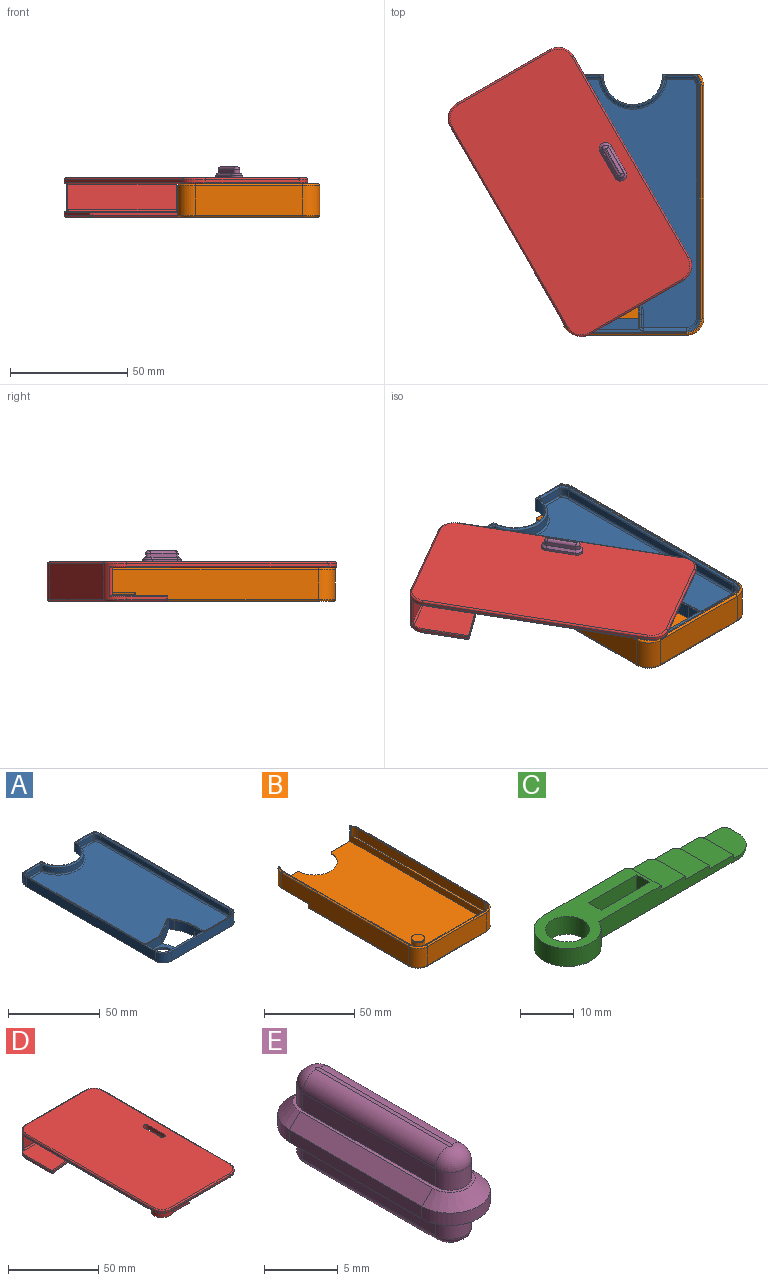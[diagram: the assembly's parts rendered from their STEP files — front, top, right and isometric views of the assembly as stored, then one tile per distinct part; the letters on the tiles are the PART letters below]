
ASSEMBLY  parts=5 mates=4
PART A: 95 faces, bbox 59.1x110.7x6.4 mm
  f0: plane 11.32x3.56mm, normal (0,-1,0), area 40.3mm2, adj f78,f79,f87,f88
  f1: plane 99.19x6.35mm, normal (1,0,0), area 629.8mm2, adj f4,f6,f36,f40
  f2: plane 15.05x6.35mm, normal (0,1,0), area 95.6mm2, adj f4,f6,f31,f37
  f3: plane 99.19x6.35mm, normal (-1,0,0), area 629.8mm2, adj f4,f6,f35,f38
  f4: plane 109.98x58.04mm, normal (0,0,-1), area 5827mm2, adj f1,f2,f3,f5,f14,f16,f17,f18
  f5: plane 15.05x6.35mm, normal (0,1,0), area 95.6mm2, adj f4,f6,f31,f41
  f6: plane 109.98x58.04mm, normal (0,0,1), area 233.7mm2, adj f1,f2,f3,f5,f11,f13,f14,f19
  f7: plane 11.32x3.56mm, normal (0,-1,0), area 40.3mm2, adj f55,f56,f66,f67
  f8: plane 105.92x53.98mm, normal (0,0,1), area 4899.9mm2, adj f44,f46,f47,f54,f55,f59,f64,f65
  f9: plane 30.16x12.91mm, normal (0,0,1), area 175.1mm2, adj f11,f13,f16,f17,f18,f19,f23,f29
  f10: plane 89.01x3.56mm, normal (1,0,0), area 316.5mm2, adj f39,f44,f45,f51
  f11: plane 25.4x5.08mm, normal (0,1,0), area 129mm2, adj f6,f9,f19,f33
  f12: plane 99.19x3.56mm, normal (-1,0,0), area 352.7mm2, adj f34,f42,f71,f94
  f13: plane 8.15x5.08mm, normal (1,0,0), area 41.4mm2, adj f6,f9,f29,f33
  f14: plane 45.97x6.35mm, normal (0,-1,0), area 291.9mm2, adj f4,f6,f35,f36
  f15: plane 18.54x3.56mm, normal (0,1,0), area 65.9mm2, adj f34,f76,f86,f91
  f16: cylinder r=7.62mm len=3.81mm, axis (0,0,1), area 5.1mm2, adj f4,f9,f17,f23
  f17: plane 1.59x1.27mm, normal (1,0,0), area 2mm2, adj f4,f9,f16,f18
  f18: plane 16.19x1.27mm, normal (0,1,0), area 20.6mm2, adj f4,f9,f17,f19
  f19: plane 6.35x6.35mm, normal (-1,0,0), area 34.3mm2, adj f4,f6,f9,f11,f18,f20
  f20: cylinder r=23.81mm len=11.91mm, axis (0,0,1), area 79.2mm2, adj f4,f6,f19,f21
  f21: plane 6.35x2.75mm, normal (-0.87,-0.5,0), area 20.2mm2, adj f4,f6,f20,f22
  f22: plane 14.02x8.1mm, normal (0.5,-0.87,0), area 102.8mm2, adj f4,f6,f21,f23,f29
  f23: plane 2.75x1.59mm, normal (0.87,0.5,0), area 4mm2, adj f4,f9,f16,f22
  f24: plane 5.59x3.56mm, normal (1,0,0), area 19.9mm2, adj f25,f75,f85,f86
  f25: cylinder r=25.08mm len=12.54mm, axis (0,0,-1), area 46.7mm2, adj f24,f26,f69,f81
  f26: plane 3.56x3.19mm, normal (0.87,0.5,0), area 13.1mm2, adj f25,f63,f64,f74
  f27: plane 13.99x8.08mm, normal (-0.5,0.87,0), area 57.5mm2, adj f53,f54,f62,f63
  f28: plane 10.06x3.56mm, normal (0,1,0), area 35.8mm2, adj f45,f46,f52,f53
  f29: plane 11.36x5.08mm, normal (0,-1,0), area 57.7mm2, adj f6,f9,f13,f22
  f30: cylinder r=4.76mm len=9.53mm, axis (0,0,1), area 38mm2, adj f4,f9
  f31: cylinder r=12.7mm len=25.4mm, axis (0,0,1), area 253.4mm2, adj f2,f4,f5,f6
  f32: cylinder r=13.97mm len=27.67mm, axis (0,0,-1), area 142.3mm2, adj f65,f66,f79,f80
  f33: cylinder r=4.76mm len=5.08mm, axis (0,0,1), area 38mm2, adj f6,f9,f11,f13
  f34: cylinder r=4.76mm len=4.76mm, axis (0,0,-1), area 26.6mm2, adj f12,f15,f70,f93
  f35: cylinder r=6.03mm len=6.35mm, axis (0,0,-1), area 60.2mm2, adj f3,f4,f6,f14
  f36: cylinder r=6.03mm len=6.35mm, axis (0,0,1), area 60.2mm2, adj f1,f4,f6,f14
  f37: plane 6.35x1.06mm, normal (-1,0,0), area 6.7mm2, adj f2,f4,f6,f38
  f38: cylinder r=6.03mm len=6.35mm, axis (0,0,-1), area 25.3mm2, adj f3,f4,f6,f37
  f39: cylinder r=4.76mm len=3.56mm, axis (0,0,-1), area 12.7mm2, adj f10,f47,f56,f57
  f40: cylinder r=6.03mm len=6.35mm, axis (0,0,-1), area 25.3mm2, adj f1,f4,f6,f41
  f41: plane 6.35x1.06mm, normal (1,0,0), area 6.7mm2, adj f4,f5,f6,f40
  f42: cylinder r=4.76mm len=3.56mm, axis (0,0,-1), area 12.7mm2, adj f12,f77,f87,f92
  f43: sphere r=0.76mm, area 0.9mm2, adj f44,f45,f46
  f44: cylinder r=0.76mm len=89.01mm, axis (0,1,0), area 106.5mm2, adj f8,f10,f43,f47
  f45: cylinder r=0.76mm len=3.56mm, axis (0,0,-1), area 4.3mm2, adj f10,f28,f43,f48
  f46: cylinder r=0.76mm len=10.06mm, axis (-1,0,0), area 12mm2, adj f8,f28,f43,f49
  f47: torus R=4mm, axis (0,0,1), area 4mm2, adj f8,f39,f44,f50
  f48: torus R=1.52mm, axis (0,0,1), area 2mm2, adj f6,f45,f51,f52
  f49: sphere r=0.76mm, area 0.3mm2, adj f46,f53,f54
  f50: sphere r=0.76mm, area 0.5mm2, adj f47,f55,f56
  f51: cylinder r=0.76mm len=89.01mm, axis (0,-1,0), area 106.5mm2, adj f6,f10,f48,f57
  f52: cylinder r=0.76mm len=10.06mm, axis (1,0,0), area 12mm2, adj f6,f28,f48,f58
  f53: cylinder r=0.76mm len=3.56mm, axis (0,0,1), area 1.4mm2, adj f27,f28,f49,f58
  f54: cylinder r=0.76mm len=14.37mm, axis (-0.87,-0.5,0), area 19.3mm2, adj f8,f27,f49,f59
  f55: cylinder r=0.76mm len=11.32mm, axis (1,0,0), area 13.5mm2, adj f7,f8,f50,f60
  f56: cylinder r=0.76mm len=3.56mm, axis (0,0,-1), area 2.2mm2, adj f7,f39,f50,f61
  f57: torus R=5.52mm, axis (0,0,1), area 4.5mm2, adj f6,f39,f51,f61
  f58: torus R=1.52mm, axis (0,0,1), area 0.7mm2, adj f6,f52,f53,f62
  f59: torus R=1.52mm, axis (0,0,1), area 2mm2, adj f8,f54,f63,f64
  f60: sphere r=0.76mm, area 0.8mm2, adj f55,f65,f66
  f61: torus R=1.52mm, axis (0,0,1), area 1mm2, adj f6,f56,f57,f67
  f62: cylinder r=0.76mm len=14.37mm, axis (0.87,0.5,0), area 19.3mm2, adj f6,f27,f58,f68
  f63: cylinder r=0.76mm len=3.56mm, axis (0,0,-1), area 4.3mm2, adj f26,f27,f59,f68
  f64: cylinder r=0.76mm len=3.57mm, axis (-0.5,0.87,0), area 4.4mm2, adj f8,f26,f59,f69
  f65: torus R=14.73mm, axis (0,0,1), area 48.9mm2, adj f8,f32,f60,f72
  f66: cylinder r=0.76mm len=3.56mm, axis (0,0,-1), area 3.9mm2, adj f7,f32,f60,f73
  f67: cylinder r=0.76mm len=11.32mm, axis (-1,0,0), area 13.5mm2, adj f6,f7,f61,f73
  f68: sphere r=0.76mm, area 0.9mm2, adj f62,f63,f74
  f69: torus R=25.84mm, axis (0,0,1), area 15.9mm2, adj f8,f25,f64,f75
  f70: torus R=4mm, axis (0,0,1), area 8.4mm2, adj f8,f34,f71,f76
  f71: cylinder r=0.76mm len=99.19mm, axis (0,-1,0), area 118.7mm2, adj f8,f12,f70,f77
  f72: sphere r=0.76mm, area 0.8mm2, adj f65,f78,f79
  f73: torus R=1.52mm, axis (0,0,1), area 1.8mm2, adj f6,f66,f67,f80
  f74: cylinder r=0.76mm len=3.57mm, axis (0.5,-0.87,0), area 4.4mm2, adj f6,f26,f68,f81
  f75: cylinder r=0.76mm len=5.59mm, axis (0,1,0), area 6.7mm2, adj f8,f24,f69,f82
  f76: cylinder r=0.76mm len=18.54mm, axis (-1,0,0), area 22.2mm2, adj f8,f15,f70,f82
  f77: torus R=4mm, axis (0,0,1), area 4mm2, adj f8,f42,f71,f83
  f78: cylinder r=0.76mm len=11.32mm, axis (1,0,0), area 13.5mm2, adj f0,f8,f72,f83
  f79: cylinder r=0.76mm len=3.56mm, axis (0,0,-1), area 3.9mm2, adj f0,f32,f72,f84
  f80: torus R=13.21mm, axis (0,0,1), area 47mm2, adj f6,f32,f73,f84
  f81: torus R=24.32mm, axis (0,0,1), area 15.5mm2, adj f6,f25,f74,f85
  f82: sphere r=0.76mm, area 0.9mm2, adj f75,f76,f86
  f83: sphere r=0.76mm, area 0.5mm2, adj f77,f78,f87
  f84: torus R=1.52mm, axis (0,0,1), area 1.8mm2, adj f6,f79,f80,f88
  f85: cylinder r=0.76mm len=5.59mm, axis (0,-1,0), area 6.7mm2, adj f6,f24,f81,f89
  f86: cylinder r=0.76mm len=3.56mm, axis (0,0,1), area 4.3mm2, adj f15,f24,f82,f89
  f87: cylinder r=0.76mm len=3.56mm, axis (0,0,-1), area 2.2mm2, adj f0,f42,f83,f90
  f88: cylinder r=0.76mm len=11.32mm, axis (-1,0,0), area 13.5mm2, adj f0,f6,f84,f90
  f89: torus R=1.52mm, axis (0,0,1), area 2mm2, adj f6,f85,f86,f91
  f90: torus R=1.52mm, axis (0,0,1), area 1mm2, adj f6,f87,f88,f92
  f91: cylinder r=0.76mm len=18.54mm, axis (1,0,0), area 22.2mm2, adj f6,f15,f89,f93
  f92: torus R=5.52mm, axis (0,0,1), area 4.5mm2, adj f6,f42,f90,f94
  f93: torus R=5.52mm, axis (0,0,1), area 9.5mm2, adj f6,f34,f91,f94
  f94: cylinder r=0.76mm len=99.19mm, axis (0,1,0), area 118.7mm2, adj f6,f12,f92,f93
PART B: 65 faces, bbox 61.8x112.7x14.2 mm
  f0: torus R=3.08mm, axis (0,0,1), area 13.2mm2, adj f28,f64
  f1: plane 14.74x10.71mm, normal (0,1,0), area 8.7mm2, adj f9,f12,f48,f55,f60,f61
  f2: plane 14.74x10.71mm, normal (0,1,0), area 8.7mm2, adj f9,f11,f39,f40,f41,f44
  f3: plane 99.19x6.35mm, normal (1,0,0), area 629.8mm2, adj f5,f6,f19,f26
  f4: plane 99.19x6.35mm, normal (-1,0,0), area 629.8mm2, adj f5,f6,f20,f25
  f5: plane 109.18x58.04mm, normal (0,0,1), area 338.3mm2, adj f3,f4,f10,f11,f12,f15,f17,f18
  f6: plane 110.21x59.06mm, normal (0,0,1), area 138.7mm2, adj f3,f4,f11,f12,f15,f19,f20,f25
  f7: plane 59.06x24.56mm, normal (0,0,-1), area 999.9mm2, adj f16,f30,f32,f41,f49,f50,f53,f55
  f8: plane 99.19x12.7mm, normal (-1,0,0), area 1201.2mm2, adj f22,f24,f30,f33,f34,f47
  f9: plane 108.71x55.5mm, normal (0,0,1), area 5723.7mm2, adj f1,f2,f10,f11,f12,f17,f18,f28
  f10: plane 45.97x4.06mm, normal (0,1,0), area 186.8mm2, adj f5,f9,f17,f18
  f11: plane 103.95x10.42mm, normal (1,0,0), area 427.6mm2, adj f2,f5,f6,f9,f17,f44,f62
  f12: plane 103.95x10.42mm, normal (-1,0,0), area 427.6mm2, adj f1,f5,f6,f9,f18,f61,f63
  f13: plane 99.19x12.7mm, normal (1,0,0), area 1218.2mm2, adj f21,f23,f43,f50,f53,f59
  f14: plane 45.97x12.7mm, normal (0,-1,0), area 583.9mm2, adj f21,f22,f35,f54
  f15: plane 45.97x6.35mm, normal (0,1,0), area 291.9mm2, adj f5,f6,f19,f20
  f16: plane 59.06x6.19mm, normal (-0.1,0.99,0), area 117.6mm2, adj f7,f30,f33,f42,f50
  f17: cylinder r=4.76mm len=4.76mm, axis (0,0,-1), area 30.4mm2, adj f5,f9,f10,f11
  f18: cylinder r=4.76mm len=4.76mm, axis (0,0,1), area 30.4mm2, adj f5,f9,f10,f12
  f19: cylinder r=6.03mm len=6.35mm, axis (0,0,-1), area 60.2mm2, adj f3,f5,f6,f15
  f20: cylinder r=6.03mm len=6.35mm, axis (0,0,1), area 60.2mm2, adj f4,f5,f6,f15
  f21: cylinder r=7.3mm len=12.7mm, axis (0,0,1), area 145.7mm2, adj f13,f14,f38,f57
  f22: cylinder r=7.3mm len=12.7mm, axis (0,0,1), area 145.7mm2, adj f8,f14,f31,f51
  f23: cylinder r=7.3mm len=9.96mm, axis (0,0,1), area 47.9mm2, adj f13,f56,f60,f61
  f24: cylinder r=7.3mm len=9.96mm, axis (0,0,1), area 47.9mm2, adj f8,f32,f39,f44
  f25: cylinder r=6.03mm len=6.35mm, axis (0,0,1), area 23.8mm2, adj f4,f5,f6,f63
  f26: cylinder r=6.03mm len=6.35mm, axis (0,0,1), area 23.8mm2, adj f3,f5,f6,f62
  f27: plane 90.59x59.06mm, normal (0,0,-1), area 5148.9mm2, adj f31,f34,f35,f38,f42,f43
  f28: cylinder r=3.84mm len=9.65mm, axis (0,0,1), area 233mm2, adj f0,f9
  f29: cylinder r=12.7mm len=25.36mm, axis (0,0,1), area 11.7mm2, adj f9,f40,f48,f49
  f30: cylinder r=0.76mm len=21.32mm, axis (0,1,0), area 24.9mm2, adj f7,f8,f16,f32,f33
  f31: torus R=6.54mm, axis (0,0,-1), area 13.2mm2, adj f22,f27,f34,f35
  f32: torus R=6.54mm, axis (0,0,1), area 5.5mm2, adj f7,f24,f30,f36
  f33: cylinder r=0.76mm len=2.74mm, axis (0,0,1), area 2.5mm2, adj f8,f16,f30,f37
  f34: cylinder r=0.76mm len=77.86mm, axis (0,-1,0), area 93.2mm2, adj f8,f27,f31,f37
  f35: cylinder r=0.76mm len=45.97mm, axis (1,0,0), area 55mm2, adj f14,f27,f31,f38
  f36: sphere r=0.76mm, area 0.5mm2, adj f32,f39,f41
  f37: sphere r=0.76mm, area 0.9mm2, adj f33,f34,f42
  f38: torus R=6.54mm, axis (0,0,-1), area 13.2mm2, adj f21,f27,f35,f43
  f39: cylinder r=0.76mm len=10.54mm, axis (0,0,1), area 7.1mm2, adj f2,f24,f36,f44
  f40: cylinder r=0.76mm len=0.76mm, axis (0,0,1), area 0.4mm2, adj f2,f9,f29,f45
  f41: cylinder r=0.76mm len=14.72mm, axis (1,0,0), area 17.6mm2, adj f2,f7,f36,f45
  f42: cylinder r=0.76mm len=59.13mm, axis (0.99,0.1,0), area 71.1mm2, adj f16,f27,f37,f46
  f43: cylinder r=0.76mm len=84.05mm, axis (0,1,0), area 100.6mm2, adj f13,f27,f38,f46
  f44: torus R=6.54mm, axis (0,0,1), area 6.1mm2, adj f2,f6,f11,f24,f39,f47
  f45: sphere r=0.76mm, area 0.9mm2, adj f40,f41,f49
  f46: sphere r=0.76mm, area 1mm2, adj f42,f43,f50
  f47: cylinder r=0.76mm len=99.19mm, axis (0,-1,0), area 118.7mm2, adj f6,f8,f44,f51
  f48: cylinder r=0.76mm len=0.76mm, axis (0,0,1), area 0.4mm2, adj f1,f9,f29,f52
  f49: torus R=13.46mm, axis (0,0,1), area 47mm2, adj f7,f29,f45,f52
  f50: cylinder r=0.76mm len=2.74mm, axis (0,0,-1), area 2.9mm2, adj f7,f13,f16,f46,f53
  f51: torus R=6.54mm, axis (0,0,1), area 13.2mm2, adj f6,f22,f47,f54
  f52: sphere r=0.76mm, area 0.9mm2, adj f48,f49,f55
  f53: cylinder r=0.76mm len=15.13mm, axis (0,1,0), area 17.5mm2, adj f7,f13,f50,f56
  f54: cylinder r=0.76mm len=45.97mm, axis (1,0,0), area 55mm2, adj f6,f14,f51,f57
  f55: cylinder r=0.76mm len=14.72mm, axis (1,0,0), area 17.6mm2, adj f1,f7,f52,f58
  f56: torus R=6.54mm, axis (0,0,1), area 5.5mm2, adj f7,f23,f53,f58
  f57: torus R=6.54mm, axis (0,0,1), area 13.2mm2, adj f6,f21,f54,f59
  f58: sphere r=0.76mm, area 0.5mm2, adj f55,f56,f60
  f59: cylinder r=0.76mm len=99.19mm, axis (0,1,0), area 118.7mm2, adj f6,f13,f57,f61
  f60: cylinder r=0.76mm len=10.54mm, axis (0,0,1), area 7.1mm2, adj f1,f23,f58,f61
  f61: torus R=6.54mm, axis (0,0,1), area 6.1mm2, adj f1,f6,f12,f23,f59,f60
  f62: cylinder r=0.76mm len=6.35mm, axis (0,0,1), area 3mm2, adj f5,f6,f11,f26
  f63: cylinder r=0.76mm len=6.35mm, axis (0,0,1), area 3mm2, adj f5,f6,f12,f25
  f64: plane 7.3x7.3mm, normal (0,0,1), area 41.8mm2, adj f0
PART C: 25 faces, bbox 53.7x12.4x4.1 mm
  f0: plane 28.38x12.45mm, normal (0,0,1), area 172.5mm2, adj f9,f10,f14,f15,f16,f17,f20,f21
  f1: plane 53.66x12.45mm, normal (0,0,-1), area 384.3mm2, adj f14,f15,f16,f17,f18,f19,f20,f21
  f2: plane 8.6x7.19mm, normal (0,0,1), area 47.9mm2, adj f6,f13,f18,f19,f20,f22,f23
  f3: plane 8.6x7.32mm, normal (0,0,1), area 54.6mm2, adj f8,f9,f10,f11,f20,f22
  f4: plane 8.6x7.32mm, normal (0,0,1), area 54.6mm2, adj f7,f8,f11,f12,f20,f22
  f5: plane 8.6x7.32mm, normal (0,0,1), area 54.6mm2, adj f6,f7,f12,f13,f20,f22
  f6: cylinder r=1.59mm len=1.46mm, axis (0,0,1), area 1.4mm2, adj f2,f5,f13,f20
  f7: cylinder r=1.59mm len=1.46mm, axis (0,0,1), area 1.4mm2, adj f4,f5,f12,f20
  f8: cylinder r=1.59mm len=1.46mm, axis (0,0,1), area 1.4mm2, adj f3,f4,f11,f20
  f9: cylinder r=1.59mm len=1.46mm, axis (0,0,1), area 1.9mm2, adj f0,f3,f10,f20
  f10: plane 7.14x1.02mm, normal (1,0,0), area 7.3mm2, adj f0,f3,f9,f22
  f11: plane 7.14x0.76mm, normal (1,0,0), area 5.4mm2, adj f3,f4,f8,f22
  f12: plane 7.14x0.76mm, normal (1,0,0), area 5.4mm2, adj f4,f5,f7,f22
  f13: plane 7.14x0.76mm, normal (1,0,0), area 5.4mm2, adj f2,f5,f6,f22
  f14: plane 4.06x3.3mm, normal (1,0,0), area 13.4mm2, adj f0,f1,f15,f16
  f15: plane 12.7x4.06mm, normal (0,-1,0), area 51.6mm2, adj f0,f1,f14,f17
  f16: plane 12.7x4.06mm, normal (0,1,0), area 51.6mm2, adj f0,f1,f14,f17
  f17: plane 4.06x3.3mm, normal (-1,0,0), area 13.4mm2, adj f0,f1,f15,f16
  f18: plane 2.06x0.76mm, normal (1,0,0), area 1.6mm2, adj f1,f2,f19,f23
  f19: cylinder r=1.46mm len=1.46mm, axis (0,0,-1), area 1.7mm2, adj f1,f2,f18,f20
  f20: plane 45.97x4.06mm, normal (0,1,0), area 134.1mm2, adj f0,f1,f2,f3,f4,f5,f6,f7
  f21: cylinder r=6.22mm len=12.45mm, axis (0,0,-1), area 109.2mm2, adj f0,f1,f20,f22
  f22: plane 36.61x4.06mm, normal (0,-1,0), area 111.1mm2, adj f0,f1,f2,f3,f4,f5,f10,f11
  f23: cylinder r=5.08mm len=5.08mm, axis (0,0,1), area 6.1mm2, adj f1,f2,f18,f22
  f24: cylinder r=4.1mm len=8.19mm, axis (0,0,1), area 104.6mm2, adj f0,f1
PART D: 82 faces, bbox 61.8x115x16.8 mm
  f0: cylinder r=1.27mm len=1.4mm, axis (0,1,0), area 1.2mm2, adj f1,f12,f19,f66
  f1: plane 12.7x3.3mm, normal (0,0,-1), area 3.6mm2, adj f0,f16,f17,f18,f19,f66,f67,f68
  f2: plane 5.12x3.05mm, normal (-1,0,0), area 15.6mm2, adj f26,f66,f68,f72
  f3: plane 0.69x0.28mm, normal (0,0,1), area 0.1mm2, adj f5,f33,f76
  f4: plane 0.69x0.28mm, normal (0,0,1), area 0.1mm2, adj f6,f48,f76
  f5: cylinder r=0.76mm len=13.13mm, axis (0,0,1), area 16.4mm2, adj f3,f10,f12,f33,f40,f75,f76,f77
  f6: cylinder r=0.76mm len=13.13mm, axis (0,0,1), area 16.2mm2, adj f4,f23,f48,f75,f76,f78,f79
  f7: torus R=4.73mm, axis (0,0,1), area 20.7mm2, adj f26,f64
  f8: plane 13.47x1.09mm, normal (1,0,0), area 14.7mm2, adj f23,f34,f41,f46
  f9: plane 19.66x1.09mm, normal (-1,0,0), area 21.5mm2, adj f10,f30,f36,f37
  f10: cylinder r=7.3mm len=15.24mm, axis (0,0,1), area 74.8mm2, adj f5,f9,f11,f20,f28,f33,f40,f56
  f11: plane 99.19x1.02mm, normal (-1,0,0), area 100.8mm2, adj f10,f21,f43,f54
  f12: plane 110.96x59.06mm, normal (0,0,-1), area 6268mm2, adj f0,f5,f16,f17,f18,f19,f25,f40
  f13: plane 45.97x1.02mm, normal (0,-1,0), area 46.7mm2, adj f21,f22,f47,f53
  f14: plane 99.19x1.02mm, normal (1,0,0), area 100.8mm2, adj f22,f23,f50,f57
  f15: plane 112.27x59.06mm, normal (0,0,1), area 6545mm2, adj f52,f53,f54,f55,f56,f57,f58,f59
  f16: plane 15.24x1.27mm, normal (0,1,0), area 16.8mm2, adj f1,f12,f17,f18
  f17: cylinder r=1.27mm len=1.27mm, axis (0,1,0), area 0.3mm2, adj f1,f12,f16,f68
  f18: cylinder r=1.27mm len=4.57mm, axis (0,-1,0), area 7.5mm2, adj f1,f12,f16,f19
  f19: cylinder r=1.27mm len=15.24mm, axis (-1,0,0), area 27.2mm2, adj f0,f1,f12,f18
  f20: plane 45.97x15.24mm, normal (0,1,0), area 700.6mm2, adj f10,f23,f29,f58
  f21: cylinder r=7.3mm len=7.3mm, axis (0,0,-1), area 11.7mm2, adj f11,f13,f45,f52
  f22: cylinder r=7.3mm len=7.3mm, axis (0,0,-1), area 11.7mm2, adj f13,f14,f49,f55
  f23: cylinder r=7.3mm len=15.24mm, axis (0,0,1), area 74.8mm2, adj f6,f8,f14,f20,f31,f48,f51,f59
  f24: plane 59.06x26.2mm, normal (0,0,-1), area 1346.3mm2, adj f28,f29,f30,f31,f34,f35
  f25: cylinder r=6.1mm len=12.19mm, axis (0,0,-1), area 173.9mm2, adj f12,f26,f66,f68,f80,f81
  f26: plane 14.95x12.19mm, normal (0,0,-1), area 55.7mm2, adj f2,f7,f25,f66,f68,f80
  f27: plane 59.06x6.19mm, normal (0.1,-0.99,0), area 64.9mm2, adj f35,f36,f41,f42
  f28: torus R=6.54mm, axis (0,0,-1), area 13.2mm2, adj f10,f24,f29,f30
  f29: cylinder r=0.76mm len=45.97mm, axis (-1,0,0), area 55mm2, adj f20,f24,f28,f31
  f30: cylinder r=0.76mm len=19.66mm, axis (0,1,0), area 23.5mm2, adj f9,f24,f28,f32
  f31: torus R=6.54mm, axis (0,0,-1), area 13.2mm2, adj f23,f24,f29,f34
  f32: sphere r=0.76mm, area 1mm2, adj f30,f35,f36
  f33: torus R=6.54mm, axis (0,0,1), area 4.7mm2, adj f3,f5,f10,f37,f74,f76
  f34: cylinder r=0.76mm len=13.47mm, axis (0,1,0), area 16.1mm2, adj f8,f24,f31,f38
  f35: cylinder r=0.76mm len=59.13mm, axis (0.99,0.1,0), area 71.1mm2, adj f24,f27,f32,f38
  f36: cylinder r=0.76mm len=1.09mm, axis (0,0,1), area 1.4mm2, adj f9,f27,f32,f39
  f37: cylinder r=0.76mm len=19.66mm, axis (0,-1,0), area 10.9mm2, adj f9,f33,f39,f74
  f38: sphere r=0.76mm, area 0.9mm2, adj f34,f35,f41
  f39: sphere r=0.76mm, area 0.6mm2, adj f36,f37,f42,f74
  f40: torus R=6.54mm, axis (0,0,1), area 8.2mm2, adj f5,f10,f12,f43
  f41: cylinder r=0.76mm len=1.09mm, axis (0,0,-1), area 1.2mm2, adj f8,f27,f38,f44
  f42: cylinder r=0.76mm len=59.08mm, axis (0.99,0.1,0), area 33mm2, adj f27,f39,f44,f74
  f43: cylinder r=0.76mm len=99.19mm, axis (0,-1,0), area 118.7mm2, adj f11,f12,f40,f45
  f44: sphere r=0.76mm, area 0.6mm2, adj f41,f42,f46,f74
  f45: torus R=6.54mm, axis (0,0,1), area 13.2mm2, adj f12,f21,f43,f47
  f46: cylinder r=0.76mm len=13.47mm, axis (0,1,0), area 7.5mm2, adj f8,f44,f48,f74
  f47: cylinder r=0.76mm len=45.97mm, axis (1,0,0), area 55mm2, adj f12,f13,f45,f49
  f48: torus R=6.54mm, axis (0,0,1), area 4.7mm2, adj f4,f6,f23,f46,f74,f76
  f49: torus R=6.54mm, axis (0,0,1), area 13.2mm2, adj f12,f22,f47,f50
  f50: cylinder r=0.76mm len=99.19mm, axis (0,1,0), area 118.7mm2, adj f12,f14,f49,f51
  f51: torus R=6.54mm, axis (0,0,1), area 8mm2, adj f12,f23,f50,f79
  f52: torus R=6.54mm, axis (0,0,1), area 13.2mm2, adj f15,f21,f53,f54
  f53: cylinder r=0.76mm len=45.97mm, axis (-1,0,0), area 55mm2, adj f13,f15,f52,f55
  f54: cylinder r=0.76mm len=99.19mm, axis (0,1,0), area 118.7mm2, adj f11,f15,f52,f56
  f55: torus R=6.54mm, axis (0,0,1), area 13.2mm2, adj f15,f22,f53,f57
  f56: torus R=6.54mm, axis (0,0,1), area 13.2mm2, adj f10,f15,f54,f58
  f57: cylinder r=0.76mm len=99.19mm, axis (0,-1,0), area 118.7mm2, adj f14,f15,f55,f59
  f58: cylinder r=0.76mm len=45.97mm, axis (1,0,0), area 55mm2, adj f15,f20,f56,f59
  f59: torus R=6.54mm, axis (0,0,1), area 13.2mm2, adj f15,f23,f57,f58
  f60: plane 12.7x2.54mm, normal (-1,0,0), area 32.3mm2, adj f12,f15,f61,f63
  f61: cylinder r=1.59mm len=3.18mm, axis (0,0,1), area 12.7mm2, adj f12,f15,f60,f62
  f62: plane 12.7x2.54mm, normal (1,0,0), area 32.3mm2, adj f12,f15,f61,f63
  f63: cylinder r=1.59mm len=3.18mm, axis (0,0,1), area 12.7mm2, adj f12,f15,f60,f62
  f64: cylinder r=4.1mm len=8.19mm, axis (0,0,1), area 118.7mm2, adj f7,f65
  f65: plane 8.19x8.19mm, normal (0,0,-1), area 52.7mm2, adj f64
  f66: plane 15.21x10.07mm, normal (0,-1,0), area 122.7mm2, adj f0,f1,f2,f12,f25,f26,f67,f70
  f67: plane 8.8x3.05mm, normal (1,0,0), area 26.8mm2, adj f1,f66,f68,f71
  f68: plane 16.05x10.07mm, normal (0,1,0), area 126.9mm2, adj f1,f2,f12,f17,f25,f26,f67,f73
  f69: plane 11.18x1.78mm, normal (0,0,-1), area 19.9mm2, adj f70,f71,f72,f73
  f70: cylinder r=0.76mm len=12.45mm, axis (1,0,0), area 8.9mm2, adj f66,f69,f71,f72
  f71: cylinder r=0.76mm len=3.05mm, axis (0,1,0), area 1.8mm2, adj f67,f69,f70,f73
  f72: cylinder r=0.76mm len=3.05mm, axis (0,-1,0), area 1.8mm2, adj f2,f69,f70,f73
  f73: cylinder r=0.76mm len=12.45mm, axis (-1,0,0), area 8.9mm2, adj f68,f69,f71,f72
  f74: plane 60.19x24.61mm, normal (0,0,1), area 1291mm2, adj f33,f37,f39,f42,f44,f46,f48,f76
  f75: plane 53.69x10.85mm, normal (0,-1,0), area 582.4mm2, adj f5,f6,f76,f77
  f76: cylinder r=0.76mm len=57.17mm, axis (1,0,0), area 65.9mm2, adj f3,f4,f5,f6,f33,f48,f74,f75
  f77: cylinder r=0.25mm len=53.8mm, axis (1,0,0), area 21.4mm2, adj f5,f12,f75,f78
  f78: torus R=1.02mm, axis (0,0,1), area 0.1mm2, adj f6,f12,f77,f79
  f79: bspline ~1.34x1.02mm, area 0.3mm2, adj f6,f51,f78
  f80: plane 3.68x0mm, normal (-1,0,0), area 0mm2, adj f25,f26,f68,f81
  f81: plane 0x0mm, normal (0,0,-1), area 0mm2, adj f25,f68,f80
PART E: 28 faces, bbox 5.4x18.1x7.3 mm
  f0: plane 12.7x1.46mm, normal (1,0,0), area 18.5mm2, adj f1,f3,f9,f20
  f1: cylinder r=1.44mm len=2.87mm, axis (0,0,-1), area 6.6mm2, adj f0,f2,f9,f22
  f2: plane 12.7x1.46mm, normal (-1,0,0), area 18.5mm2, adj f1,f3,f9,f23
  f3: cylinder r=1.44mm len=2.87mm, axis (0,0,-1), area 6.6mm2, adj f0,f2,f9,f21
  f4: plane 13.03x0.33mm, normal (0,0,1), area 4.3mm2, adj f20,f21,f22,f23
  f5: plane 12.7x1.02mm, normal (1,0,0), area 12.9mm2, adj f6,f8,f10,f19
  f6: cylinder r=2.71mm len=5.41mm, axis (0,0,-1), area 8.6mm2, adj f5,f7,f10,f17
  f7: plane 12.7x1.02mm, normal (-1,0,0), area 12.9mm2, adj f6,f8,f10,f16
  f8: cylinder r=2.71mm len=5.41mm, axis (0,0,-1), area 8.6mm2, adj f5,f7,f10,f18
  f9: plane 16.08x3.38mm, normal (0,0,1), area 8.9mm2, adj f0,f1,f2,f3,f16,f17,f18,f19
  f10: plane 18.11x5.41mm, normal (0,0,-1), area 48.8mm2, adj f5,f6,f7,f8,f12,f13,f14,f15
  f11: plane 14.55x1.85mm, normal (0,0,-1), area 26.2mm2, adj f24,f25,f26,f27
  f12: cylinder r=1.44mm len=2.87mm, axis (0,0,-1), area 9.2mm2, adj f10,f13,f15,f25
  f13: plane 12.7x2.03mm, normal (-1,0,0), area 25.8mm2, adj f10,f12,f14,f27
  f14: cylinder r=1.44mm len=2.87mm, axis (0,0,-1), area 9.2mm2, adj f10,f13,f15,f26
  f15: plane 12.7x2.03mm, normal (1,0,0), area 25.8mm2, adj f10,f12,f14,f24
  f16: plane 12.7x1.02mm, normal (-0.71,0,0.71), area 18.2mm2, adj f7,f9,f17,f18
  f17: cone r=1.69mm half-angle=45deg, axis (0,0,-1), area 9.9mm2, adj f6,f9,f16,f19
  f18: cone r=1.69mm half-angle=45deg, axis (0,0,-1), area 9.9mm2, adj f8,f9,f16,f19
  f19: plane 12.7x1.02mm, normal (0.71,0,0.71), area 18.2mm2, adj f5,f9,f17,f18
  f20: cylinder r=1.27mm len=12.7mm, axis (0,-1,0), area 25.3mm2, adj f0,f4,f21,f22
  f21: torus R=0.17mm, axis (0,0,1), area 6.1mm2, adj f3,f4,f20,f23
  f22: torus R=0.17mm, axis (0,0,1), area 6.1mm2, adj f1,f4,f20,f23
  f23: cylinder r=1.27mm len=12.7mm, axis (0,1,0), area 25.3mm2, adj f2,f4,f21,f22
  f24: cylinder r=0.51mm len=12.7mm, axis (0,1,0), area 10.1mm2, adj f11,f15,f25,f26
  f25: torus R=0.93mm, axis (0,0,1), area 3.1mm2, adj f11,f12,f24,f27
  f26: torus R=0.93mm, axis (0,0,1), area 3.1mm2, adj f11,f14,f24,f27
  f27: cylinder r=0.51mm len=12.7mm, axis (0,-1,0), area 10.1mm2, adj f11,f13,f25,f26
PLACE A t=(-0.35,14.18,3.81)mm
PLACE B t=(-0.35,14.18,3.81)mm
PLACE C rot(axis=(0,0,1),30deg) t=(-28.2,18.19,3.81)mm
PLACE D rot(axis=(0,0,1),30deg) t=(-28.2,18.19,3.81)mm
PLACE E rot(axis=(0,0,1),30deg) t=(-28.2,18.19,3.81)mm
MATE fastened E.f1 <-> D.f61  axis (0,0,-1) through (-12.02,34.86,14.22)mm
MATE fastened C.f1 <-> D.f69  axis (0,0,-1) through (-9.48,-26.89,3.81)mm
MATE revolute B.f0 <-> C.f21  axis (0,0,1) through (-21.75,-35.79,3.81)mm
MATE fastened A.f14 <-> B.f15  axis (0,-1,0) through (-0.35,-43.41,14.22)mm
